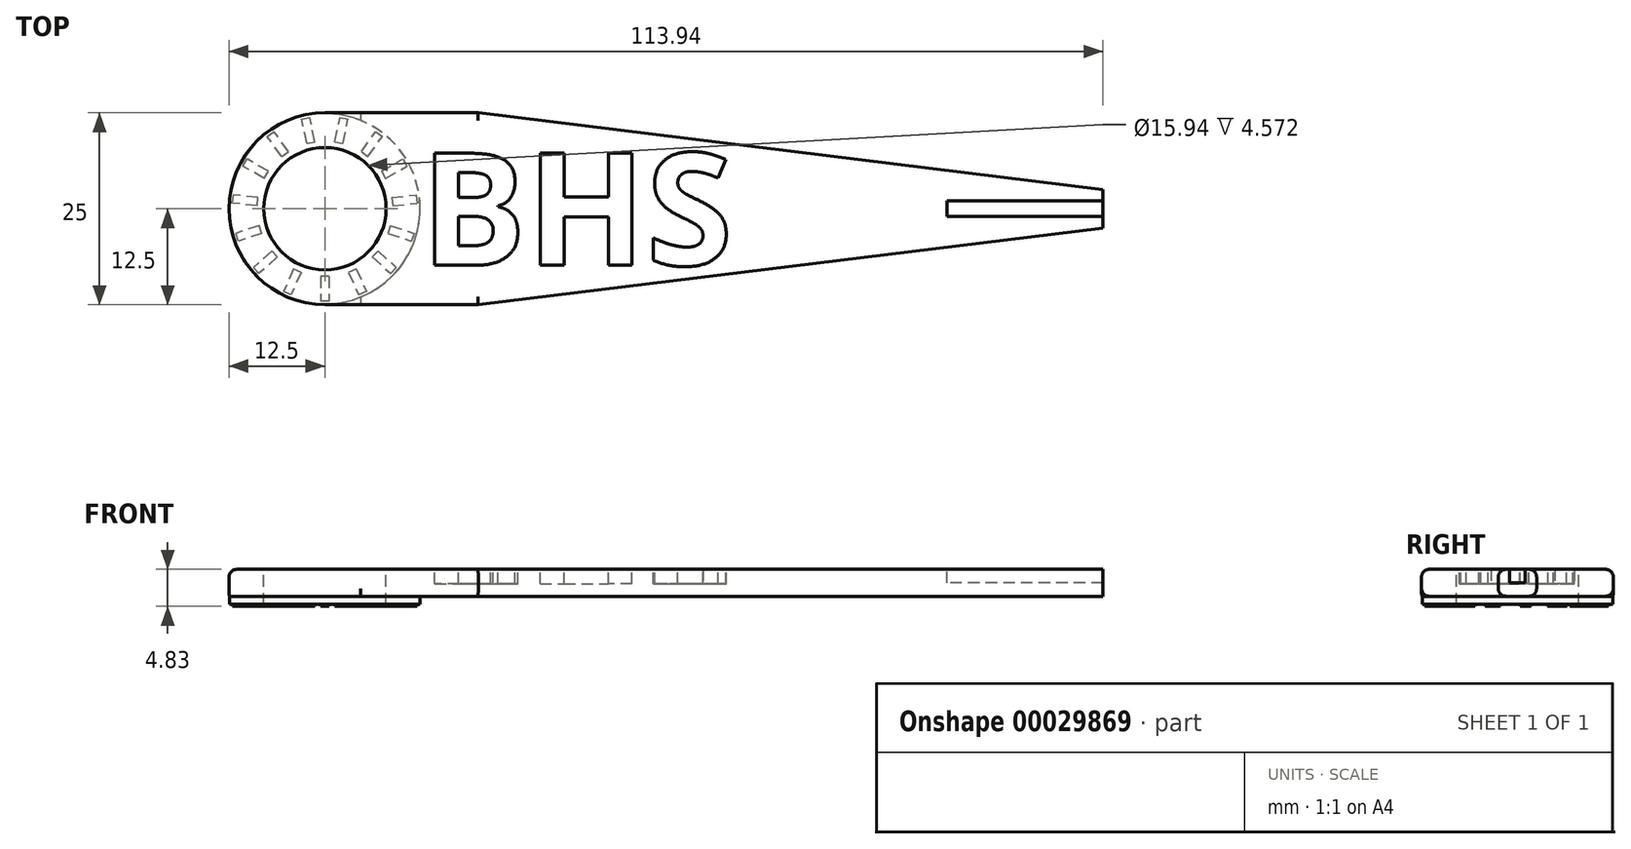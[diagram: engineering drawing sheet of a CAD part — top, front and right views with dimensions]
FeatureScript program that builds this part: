
annotation { "Feature Type Name" : "Feature", "Feature Type Description" : "" }
export const myFeature = defineFeature(function(context is Context, id is Id, definition is map)
    precondition{}
    {
        {
            var Q0;
            Q0=qCreatedBy(makeId("Top.planeOp"),FACE);
            var sketch = newSketch(context, id + "F0", { "sketchPlane" : qUnion([Q0])});
            skCircle(sketch, "E0", {"center": v(0, 0) * mm, "radius": 8 * mm});
            skCircle(sketch, "E1.0", {"center": v(0, 0) * mm, "radius": 12.5 * mm});
            skLineSegment(sketch, "E2", {"start": v(0, 12.5) * mm, "end": v(20, 12.5) * mm});
            skLineSegment(sketch, "E3", {"start": v(0, -12.5) * mm, "end": v(20, -12.5) * mm});
            skLineSegment(sketch, "E4", {"start": v(20, 12.5) * mm, "end": v(101.44, 2.5) * mm});
            skLineSegment(sketch, "E5", {"start": v(20, -12.5) * mm, "end": v(101.44, -2.5) * mm});
            skLineSegment(sketch, "E6", {"start": v(101.44, -2.5) * mm, "end": v(101.44, 2.5) * mm});
            skLineSegment(sketch, "E7", {"start": v(20, 12.5) * mm, "end": v(112.96, 12.5) * mm, "construction": true});
            skSolve(sketch);
        }
        {
            var Q0;
            Q0 = qSketchRegion(id + "F0", true);
            extrude(context, id + "F1", {"entities" : qUnion([Q0]), "depth" : 3.5 * mm});
        }
        {
            var Q0;
            Q0=makeQuery(id+"F1.opExtrude","CAP_FACE",FACE,{"disambiguationData":[OSD([sQuery(id+"F0.wireOp",EDGE,"E0"),sQuery(id+"F0.wireOp",EDGE,"E1.0"),sQuery(id+"F0.wireOp",EDGE,"E2"),sQuery(id+"F0.wireOp",EDGE,"E3"),sQuery(id+"F0.wireOp",EDGE,"E4"),sQuery(id+"F0.wireOp",EDGE,"E5"),sQuery(id+"F0.wireOp",EDGE,"E6")])],"isStart":false});
            var sketch = newSketch(context, id + "F2", { "sketchPlane" : qUnion([Q0])});
            skCircle(sketch, "E8", {"center": v(0, 0) * mm, "radius": 7.97 * mm});
            skCircle(sketch, "E9", {"center": v(0, 0) * mm, "radius": 12.42 * mm});
            skSolve(sketch);
        }
        {
            var Q0;
            Q0 = qSketchRegion(id + "F2", true);
            extrude(context, id + "F3", {"entities" : qUnion([Q0]), "operationType" : NewBodyOperationType.ADD, "oppositeDirection" : true, "depth" : 4.57 * mm});
        }
        {
            var Q0;
            Q0=makeQuery(id+"F3.opExtrude","CAP_FACE",FACE,{"disambiguationData":[OSD([sQuery(id+"F2.wireOp",EDGE,"E8"),sQuery(id+"F2.wireOp",EDGE,"E9")])],"isStart":false});
            var sketch = newSketch(context, id + "F4", { "sketchPlane" : qUnion([Q0])});
            skLineSegment(sketch, "E10.rect.bottom", {"start": v(0.54, 8.82) * mm, "end": v(-0.54, 8.82) * mm});
            skLineSegment(sketch, "E10.rect.top", {"start": v(0.54, 12.04) * mm, "end": v(-0.54, 12.04) * mm});
            skLineSegment(sketch, "E10.rect.left", {"start": v(0.54, 8.82) * mm, "end": v(0.54, 12.04) * mm});
            skLineSegment(sketch, "E10.rect.right", {"start": v(-0.54, 8.82) * mm, "end": v(-0.54, 12.04) * mm});
            skPoint(sketch, "E10.rect.middle", {"position": v(0, 10.43) * mm});
            skLineSegment(sketch, "E11.1.0", {"start": v(-3.1, 8.28) * mm, "end": v(-4.08, 7.84) * mm});
            skLineSegment(sketch, "E11.1.1", {"start": v(-3.1, 8.28) * mm, "end": v(-4.4, 11.22) * mm});
            skPoint(sketch, "E11.1.2", {"position": v(-4.24, 9.53) * mm});
            skLineSegment(sketch, "E11.1.3", {"start": v(-4.08, 7.84) * mm, "end": v(-5.39, 10.78) * mm});
            skLineSegment(sketch, "E11.1.4", {"start": v(-4.4, 11.22) * mm, "end": v(-5.39, 10.78) * mm});
            skLineSegment(sketch, "E11.2.0", {"start": v(-6.2, 6.3) * mm, "end": v(-6.92, 5.5) * mm});
            skLineSegment(sketch, "E11.2.1", {"start": v(-6.2, 6.3) * mm, "end": v(-8.6, 8.46) * mm});
            skPoint(sketch, "E11.2.2", {"position": v(-7.75, 6.98) * mm});
            skLineSegment(sketch, "E11.2.3", {"start": v(-6.92, 5.5) * mm, "end": v(-9.3, 7.66) * mm});
            skLineSegment(sketch, "E11.2.4", {"start": v(-8.6, 8.46) * mm, "end": v(-9.3, 7.66) * mm});
            skPoint(sketch, "E11.center", {"position": v(0, 0) * mm});
            skLineSegment(sketch, "E12.2.3.0", {"start": v(-8.23, 3.24) * mm, "end": v(-8.56, 2.22) * mm});
            skLineSegment(sketch, "E12.3.3.0", {"start": v(-8.23, 3.24) * mm, "end": v(-11.29, 4.23) * mm});
            skPoint(sketch, "E12.6.3.0", {"position": v(-9.92, 3.22) * mm});
            skLineSegment(sketch, "E12.7.3.0", {"start": v(-8.56, 2.22) * mm, "end": v(-11.62, 3.21) * mm});
            skLineSegment(sketch, "E12.10.3.0", {"start": v(-11.29, 4.23) * mm, "end": v(-11.62, 3.21) * mm});
            skLineSegment(sketch, "E13.2.4.0", {"start": v(-8.83, -0.39) * mm, "end": v(-8.72, -1.46) * mm});
            skLineSegment(sketch, "E13.3.4.0", {"start": v(-8.83, -0.39) * mm, "end": v(-12.03, -0.73) * mm});
            skPoint(sketch, "E13.6.4.0", {"position": v(-10.38, -1.1) * mm});
            skLineSegment(sketch, "E13.7.4.0", {"start": v(-8.72, -1.46) * mm, "end": v(-11.92, -1.8) * mm});
            skLineSegment(sketch, "E13.10.4.0", {"start": v(-12.03, -0.73) * mm, "end": v(-11.92, -1.8) * mm});
            skLineSegment(sketch, "E13.2.5.0", {"start": v(-7.91, -3.95) * mm, "end": v(-7.37, -4.88) * mm});
            skLineSegment(sketch, "E13.3.5.0", {"start": v(-7.91, -3.95) * mm, "end": v(-10.7, -5.56) * mm});
            skPoint(sketch, "E13.6.5.0", {"position": v(-9.04, -5.22) * mm});
            skLineSegment(sketch, "E13.7.5.0", {"start": v(-7.37, -4.88) * mm, "end": v(-10.16, -6.49) * mm});
            skLineSegment(sketch, "E13.10.5.0", {"start": v(-10.7, -5.56) * mm, "end": v(-10.16, -6.49) * mm});
            skLineSegment(sketch, "E13.2.6.0", {"start": v(-5.62, -6.82) * mm, "end": v(-4.75, -7.45) * mm});
            skLineSegment(sketch, "E13.3.6.0", {"start": v(-5.62, -6.82) * mm, "end": v(-7.51, -9.43) * mm});
            skPoint(sketch, "E13.6.6.0", {"position": v(-6.13, -8.44) * mm});
            skLineSegment(sketch, "E13.7.6.0", {"start": v(-4.75, -7.45) * mm, "end": v(-6.65, -10.06) * mm});
            skLineSegment(sketch, "E13.10.6.0", {"start": v(-7.51, -9.43) * mm, "end": v(-6.65, -10.06) * mm});
            skLineSegment(sketch, "E13.2.7.0", {"start": v(-2.36, -8.52) * mm, "end": v(-1.3, -8.74) * mm});
            skLineSegment(sketch, "E13.3.7.0", {"start": v(-2.36, -8.52) * mm, "end": v(-3.03, -11.67) * mm});
            skPoint(sketch, "E13.6.7.0", {"position": v(-2.17, -10.2) * mm});
            skLineSegment(sketch, "E13.7.7.0", {"start": v(-1.3, -8.74) * mm, "end": v(-1.98, -11.9) * mm});
            skLineSegment(sketch, "E13.10.7.0", {"start": v(-3.03, -11.67) * mm, "end": v(-1.98, -11.9) * mm});
            skLineSegment(sketch, "E13.2.8.0", {"start": v(1.3, -8.74) * mm, "end": v(2.36, -8.52) * mm});
            skLineSegment(sketch, "E13.3.8.0", {"start": v(1.3, -8.74) * mm, "end": v(1.98, -11.9) * mm});
            skPoint(sketch, "E13.6.8.0", {"position": v(2.17, -10.2) * mm});
            skLineSegment(sketch, "E13.7.8.0", {"start": v(2.36, -8.52) * mm, "end": v(3.03, -11.67) * mm});
            skLineSegment(sketch, "E13.10.8.0", {"start": v(1.98, -11.9) * mm, "end": v(3.03, -11.67) * mm});
            skLineSegment(sketch, "E13.2.9.0", {"start": v(4.75, -7.45) * mm, "end": v(5.62, -6.82) * mm});
            skLineSegment(sketch, "E13.3.9.0", {"start": v(4.75, -7.45) * mm, "end": v(6.65, -10.06) * mm});
            skPoint(sketch, "E13.6.9.0", {"position": v(6.13, -8.44) * mm});
            skLineSegment(sketch, "E13.7.9.0", {"start": v(5.62, -6.82) * mm, "end": v(7.51, -9.43) * mm});
            skLineSegment(sketch, "E13.10.9.0", {"start": v(6.65, -10.06) * mm, "end": v(7.51, -9.43) * mm});
            skLineSegment(sketch, "E13.2.10.0", {"start": v(7.37, -4.88) * mm, "end": v(7.91, -3.95) * mm});
            skLineSegment(sketch, "E13.3.10.0", {"start": v(7.37, -4.88) * mm, "end": v(10.16, -6.49) * mm});
            skPoint(sketch, "E13.6.10.0", {"position": v(9.04, -5.22) * mm});
            skLineSegment(sketch, "E13.7.10.0", {"start": v(7.91, -3.95) * mm, "end": v(10.7, -5.56) * mm});
            skLineSegment(sketch, "E13.10.10.0", {"start": v(10.16, -6.49) * mm, "end": v(10.7, -5.56) * mm});
            skLineSegment(sketch, "E13.2.11.0", {"start": v(8.72, -1.46) * mm, "end": v(8.83, -0.39) * mm});
            skLineSegment(sketch, "E13.3.11.0", {"start": v(8.72, -1.46) * mm, "end": v(11.92, -1.8) * mm});
            skPoint(sketch, "E13.6.11.0", {"position": v(10.38, -1.1) * mm});
            skLineSegment(sketch, "E13.7.11.0", {"start": v(8.83, -0.39) * mm, "end": v(12.03, -0.73) * mm});
            skLineSegment(sketch, "E13.10.11.0", {"start": v(11.92, -1.8) * mm, "end": v(12.03, -0.73) * mm});
            skLineSegment(sketch, "E13.2.12.0", {"start": v(8.56, 2.22) * mm, "end": v(8.23, 3.24) * mm});
            skLineSegment(sketch, "E13.3.12.0", {"start": v(8.56, 2.22) * mm, "end": v(11.62, 3.21) * mm});
            skPoint(sketch, "E13.6.12.0", {"position": v(9.92, 3.22) * mm});
            skLineSegment(sketch, "E13.7.12.0", {"start": v(8.23, 3.24) * mm, "end": v(11.29, 4.23) * mm});
            skLineSegment(sketch, "E13.10.12.0", {"start": v(11.62, 3.21) * mm, "end": v(11.29, 4.23) * mm});
            skLineSegment(sketch, "E13.2.13.0", {"start": v(6.92, 5.5) * mm, "end": v(6.2, 6.3) * mm});
            skLineSegment(sketch, "E13.3.13.0", {"start": v(6.92, 5.5) * mm, "end": v(9.3, 7.66) * mm});
            skPoint(sketch, "E13.6.13.0", {"position": v(7.75, 6.98) * mm});
            skLineSegment(sketch, "E13.7.13.0", {"start": v(6.2, 6.3) * mm, "end": v(8.6, 8.46) * mm});
            skLineSegment(sketch, "E13.10.13.0", {"start": v(9.3, 7.66) * mm, "end": v(8.6, 8.46) * mm});
            skLineSegment(sketch, "E13.2.14.0", {"start": v(4.08, 7.84) * mm, "end": v(3.1, 8.28) * mm});
            skLineSegment(sketch, "E13.3.14.0", {"start": v(4.08, 7.84) * mm, "end": v(5.39, 10.78) * mm});
            skPoint(sketch, "E13.6.14.0", {"position": v(4.24, 9.53) * mm});
            skLineSegment(sketch, "E13.7.14.0", {"start": v(3.1, 8.28) * mm, "end": v(4.4, 11.22) * mm});
            skLineSegment(sketch, "E13.10.14.0", {"start": v(5.39, 10.78) * mm, "end": v(4.4, 11.22) * mm});
            skSolve(sketch);
        }
        {
            var Q0;
            Q0 = qSketchRegion(id + "F4", true);
            extrude(context, id + "F5", {"entities" : qUnion([Q0]), "operationType" : NewBodyOperationType.ADD, "depth" : 0.25 * mm});
        }
        {
            var Q0;
            Q0=makeQuery(id+"F1.opExtrude","CAP_FACE",FACE,{"disambiguationData":[OSD([sQuery(id+"F0.wireOp",EDGE,"E0"),sQuery(id+"F0.wireOp",EDGE,"E1.0"),sQuery(id+"F0.wireOp",EDGE,"E2"),sQuery(id+"F0.wireOp",EDGE,"E3"),sQuery(id+"F0.wireOp",EDGE,"E4"),sQuery(id+"F0.wireOp",EDGE,"E5"),sQuery(id+"F0.wireOp",EDGE,"E6")])],"isStart":false});
            var sketch = newSketch(context, id + "F6", { "sketchPlane" : qUnion([Q0])});
            skLineSegment(sketch, "E14.bottom", {"start": v(101.44, 1) * mm, "end": v(81.12, 1) * mm});
            skLineSegment(sketch, "E14.top", {"start": v(101.44, -1) * mm, "end": v(81.12, -1) * mm});
            skLineSegment(sketch, "E14.left", {"start": v(101.44, 1) * mm, "end": v(101.44, -1) * mm});
            skLineSegment(sketch, "E14.right", {"start": v(81.12, 1) * mm, "end": v(81.12, -1) * mm});
            skSolve(sketch);
        }
        {
            var Q0;
            Q0 = qSketchRegion(id + "F6", true);
            extrude(context, id + "F7", {"entities" : qUnion([Q0]), "operationType" : NewBodyOperationType.REMOVE, "oppositeDirection" : true, "depth" : 1.78 * mm});
        }
        {
            var Q0;
            Q0=makeQuery(id+"F1.opExtrude","CAP_EDGE",EDGE,{"disambiguationData":[OSD([sQuery(id+"F0.wireOp",EDGE,"E2")])],"isStart":false});
            var Q1;
            Q1=makeQuery(id+"F1.opExtrude","CAP_EDGE",EDGE,{"disambiguationData":[OSD([sQuery(id+"F0.wireOp",EDGE,"E4")])],"isStart":false});
            var Q2;
            Q2=makeQuery(id+"F1.opExtrude","CAP_EDGE",EDGE,{"disambiguationData":[OSD([sQuery(id+"F0.wireOp",EDGE,"E5")])],"isStart":false});
            var Q3;
            Q3=makeQuery(id+"F1.opExtrude","CAP_EDGE",EDGE,{"disambiguationData":[OSD([sQuery(id+"F0.wireOp",EDGE,"E3")])],"isStart":false});
            var Q4;
            Q4=makeQuery(id+"F1.opExtrude","CAP_EDGE",EDGE,{"disambiguationData":[OSD([sQuery(id+"F0.wireOp",EDGE,"E5")])],"isStart":true});
            var Q5;
            Q5=makeQuery(id+"F1.opExtrude","CAP_EDGE",EDGE,{"disambiguationData":[OSD([sQuery(id+"F0.wireOp",EDGE,"E3")])],"isStart":true});
            var Q6;
            Q6=makeQuery(id+"F1.opExtrude","CAP_EDGE",EDGE,{"disambiguationData":[OSD([sQuery(id+"F0.wireOp",EDGE,"E1.0")])],"isStart":true});
            var Q7;
            Q7=makeQuery(id+"F1.opExtrude","CAP_EDGE",EDGE,{"disambiguationData":[OSD([sQuery(id+"F0.wireOp",EDGE,"E2")])],"isStart":true});
            var Q8;
            Q8=makeQuery(id+"F1.opExtrude","CAP_EDGE",EDGE,{"disambiguationData":[OSD([sQuery(id+"F0.wireOp",EDGE,"E1.0")])],"isStart":false});
            var Q9;
            Q9=makeQuery(id+"F1.opExtrude","CAP_EDGE",EDGE,{"disambiguationData":[OSD([sQuery(id+"F0.wireOp",EDGE,"E4")])],"isStart":true});
            fillet(context, id + "F8", {"entities" : qUnion([Q0, Q1, Q2, Q3, Q4, Q5, Q6, Q7, Q8, Q9]), "radius" : 1 * mm, "tangentPropagation" : true, "allowEdgeOverflow" : false});
        }
        {
            var Q0;
            Q0=makeQuery(id+"F2.imprint","IMPRINT",FACE,{"disambiguationData":[TD([[makeQuery(id+"F2.imprint","IMPRINT",EDGE,{"derivedFrom":sQuery(id+"F2.wireOp",EDGE,"E9")}),-1.0]])]});
            var sketch = newSketch(context, id + "F9", { "sketchPlane" : qUnion([Q0])});
            skText(sketch, "E15", { "text": "BHS", "fontName": "OpenSans-Bold.ttf"});
            const initialGuessF9  = {"E15": [0.0125, -0.00736, 1, 0, 0.01472]};
            skSetInitialGuess(sketch, initialGuessF9);
            skSolve(sketch);
        }
        {
            var Q0;
            Q0 = qSketchRegion(id + "F9", true);
            extrude(context, id + "F10", {"entities" : qUnion([Q0]), "operationType" : NewBodyOperationType.REMOVE, "oppositeDirection" : true, "depth" : 1.9 * mm});
        }
    });
